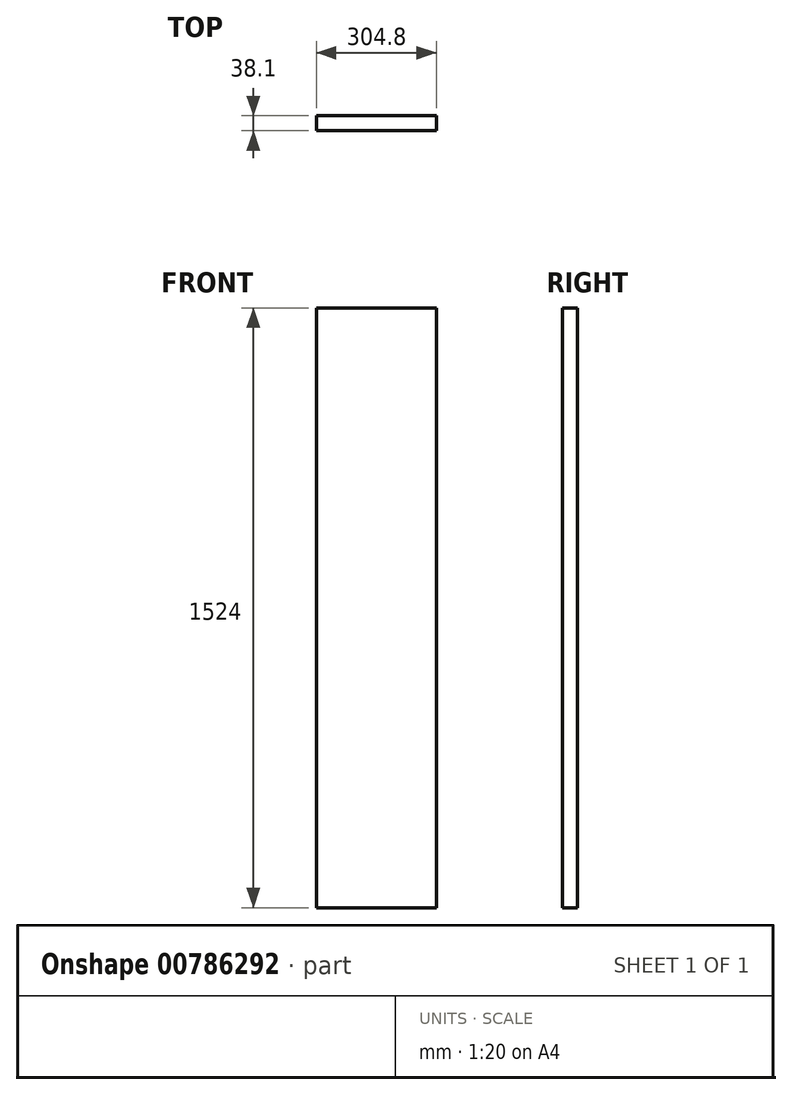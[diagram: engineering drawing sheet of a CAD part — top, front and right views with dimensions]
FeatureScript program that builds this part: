
annotation { "Feature Type Name" : "Feature", "Feature Type Description" : "" }
export const myFeature = defineFeature(function(context is Context, id is Id, definition is map)
    precondition{}
    {
        {
            var Q0;
            Q0=qCreatedBy(makeId("Front.planeOp"),FACE);
            var sketch = newSketch(context, id + "F0", { "sketchPlane" : qUnion([Q0])});
            skLineSegment(sketch, "E0.bottom", {"start": v(-152.4, 762) * mm, "end": v(152.4, 762) * mm});
            skLineSegment(sketch, "E0.top", {"start": v(-152.4, -762) * mm, "end": v(152.4, -762) * mm});
            skLineSegment(sketch, "E0.left", {"start": v(-152.4, 762) * mm, "end": v(-152.4, -762) * mm});
            skLineSegment(sketch, "E0.right", {"start": v(152.4, 762) * mm, "end": v(152.4, -762) * mm});
            skPoint(sketch, "E0.middle", {"position": v(0, 0) * mm});
            skSolve(sketch);
        }
        {
            var Q0;
            Q0=makeQuery(id+"F0.imprint","IMPRINT",FACE,{"disambiguationData":[TD([[makeQuery(id+"F0.imprint","IMPRINT",EDGE,{"derivedFrom":sQuery(id+"F0.wireOp",EDGE,"E0.bottom")}),-1.0]])]});
            extrude(context, id + "F1", {"entities" : qUnion([Q0]), "endBound" : BoundingType.SYMMETRIC, "depth" : 38.1 * mm, "offsetDistance" : 25.4 * mm});
        }
    });
